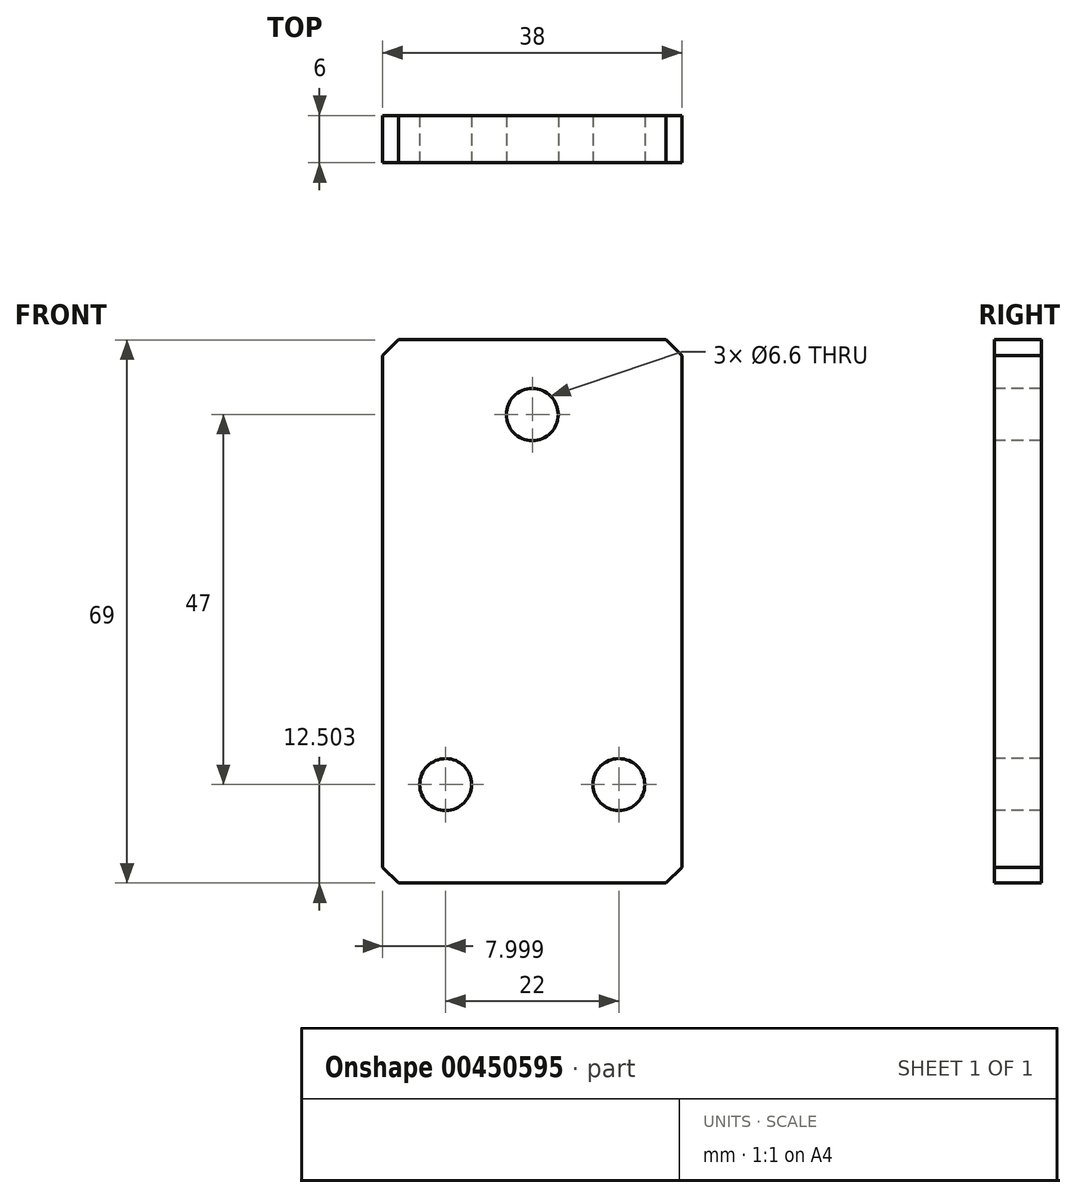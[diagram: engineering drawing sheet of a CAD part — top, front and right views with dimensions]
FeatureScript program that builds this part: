
annotation { "Feature Type Name" : "Feature", "Feature Type Description" : "" }
export const myFeature = defineFeature(function(context is Context, id is Id, definition is map)
    precondition{}
    {
        {
            var Q0;
            Q0=qCreatedBy(makeId("Front.planeOp"),FACE);
            var sketch = newSketch(context, id + "F0", { "sketchPlane" : qUnion([Q0])});
            skLineSegment(sketch, "E0", {"start": v(-4.9, -71.03) * mm, "end": v(7.1, -71.03) * mm});
            skLineSegment(sketch, "E1", {"start": v(-1.97, -61.53) * mm, "end": v(-1.97, -80.53) * mm});
            skLineSegment(sketch, "E2", {"start": v(-1.97, -130.53) * mm, "end": v(-1.97, -61.53) * mm});
            skLineSegment(sketch, "E3", {"start": v(-1.97, -61.53) * mm, "end": v(4.03, -61.53) * mm});
            skLineSegment(sketch, "E4", {"start": v(4.03, -61.53) * mm, "end": v(4.03, -130.53) * mm});
            skLineSegment(sketch, "E5", {"start": v(4.03, -130.53) * mm, "end": v(-1.97, -130.53) * mm});
            skLineSegment(sketch, "E6", {"start": v(-1.97, -105.53) * mm, "end": v(-1.97, -130.53) * mm});
            skLineSegment(sketch, "E7", {"start": v(-5.58, -118.03) * mm, "end": v(8.42, -118.03) * mm});
            skLineSegment(sketch, "E8", {"start": v(-67.54, -61.53) * mm, "end": v(-101.54, -61.53) * mm});
            skLineSegment(sketch, "E9", {"start": v(-65.54, -63.53) * mm, "end": v(-67.54, -61.53) * mm});
            skLineSegment(sketch, "E10", {"start": v(-67.54, -130.53) * mm, "end": v(-101.54, -130.53) * mm});
            skLineSegment(sketch, "E11", {"start": v(-65.54, -128.53) * mm, "end": v(-67.54, -130.53) * mm});
            skLineSegment(sketch, "E12", {"start": v(-65.54, -63.53) * mm, "end": v(-65.54, -128.53) * mm});
            skLineSegment(sketch, "E13", {"start": v(-103.54, -63.53) * mm, "end": v(-103.54, -128.53) * mm});
            skLineSegment(sketch, "E14", {"start": v(-101.54, -130.53) * mm, "end": v(-103.54, -128.53) * mm});
            skLineSegment(sketch, "E15", {"start": v(-101.54, -61.53) * mm, "end": v(-103.54, -63.53) * mm});
            skLineSegment(sketch, "E16", {"start": v(-89.1, -71.03) * mm, "end": v(-80, -71.03) * mm});
            skLineSegment(sketch, "E17", {"start": v(-84.54, -75.58) * mm, "end": v(-84.54, -66.48) * mm});
            skLineSegment(sketch, "E18", {"start": v(-78.1, -118.03) * mm, "end": v(-69, -118.03) * mm});
            skLineSegment(sketch, "E19", {"start": v(-73.54, -122.58) * mm, "end": v(-73.54, -113.48) * mm});
            skLineSegment(sketch, "E20", {"start": v(-100.1, -118.03) * mm, "end": v(-91, -118.03) * mm});
            skLineSegment(sketch, "E21", {"start": v(-95.54, -122.58) * mm, "end": v(-95.54, -113.48) * mm});
            skCircle(sketch, "E22", {"center": v(-84.54, -71.03) * mm, "radius": 3.3 * mm});
            skCircle(sketch, "E23", {"center": v(-73.54, -118.03) * mm, "radius": 3.3 * mm});
            skCircle(sketch, "E24", {"center": v(-95.54, -118.03) * mm, "radius": 3.3 * mm});
            skSolve(sketch);
        }
        {
            var Q0;
            Q0=makeQuery(id+"F0.imprint","IMPRINT",FACE,{"disambiguationData":[TD([[makeQuery(id+"F0.imprint","IMPRINT",EDGE,{"derivedFrom":sQuery(id+"F0.wireOp",EDGE,"E8")}),1.0]])]});
            extrude(context, id + "F1", {"entities" : qUnion([Q0]), "oppositeDirection" : true, "depth" : 6 * mm});
        }
    });
